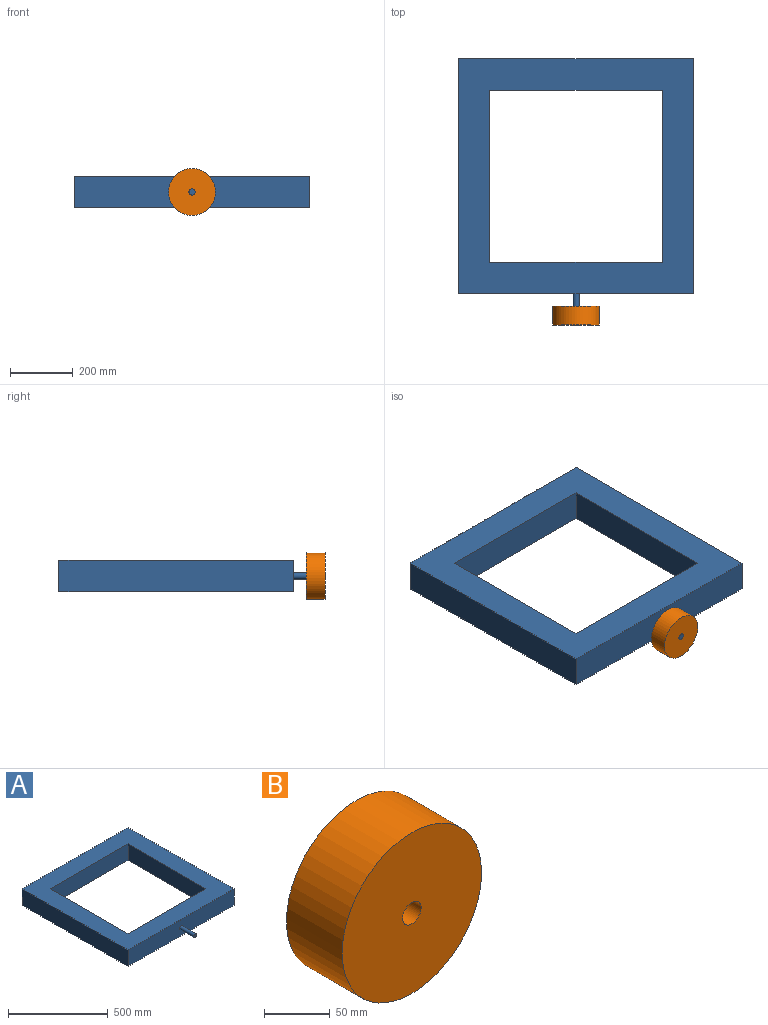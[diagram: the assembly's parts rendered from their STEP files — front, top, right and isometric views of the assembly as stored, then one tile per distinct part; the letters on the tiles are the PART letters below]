
ASSEMBLY  parts=2 mates=1
PART A: 12 faces, bbox 750x850x100 mm
  f0: plane 550x100mm, normal (0,1,0), area 55000mm2, adj f1,f7,f8,f9
  f1: plane 550x100mm, normal (1,0,0), area 55000mm2, adj f0,f2,f8,f9
  f2: plane 550x100mm, normal (0,-1,0), area 55000mm2, adj f1,f7,f8,f9
  f3: plane 750x100mm, normal (-1,0,0), area 75000mm2, adj f4,f6,f8,f9
  f4: plane 750x100mm, normal (0,-1,0), area 74685.8mm2, adj f3,f5,f8,f9,f10
  f5: plane 750x100mm, normal (1,0,0), area 75000mm2, adj f4,f6,f8,f9
  f6: plane 750x100mm, normal (0,1,0), area 75000mm2, adj f3,f5,f8,f9
  f7: plane 550x100mm, normal (-1,0,0), area 55000mm2, adj f0,f2,f8,f9
  f8: plane 750x750mm, normal (0,0,1), area 260000mm2, adj f0,f1,f2,f3,f4,f5,f6,f7
  f9: plane 750x750mm, normal (0,0,-1), area 260000mm2, adj f0,f1,f2,f3,f4,f5,f6,f7
  f10: cylinder r=10mm len=100mm, axis (0,1,0), area 6283.2mm2, adj f4,f11
  f11: plane 20x20mm, normal (0,-1,0), area 314.2mm2, adj f10
PART B: 4 faces, bbox 150x60x150 mm
  f0: plane 150x150mm, normal (0,1,0), area 17357.3mm2, adj f2,f3
  f1: plane 150x150mm, normal (0,-1,0), area 17357.3mm2, adj f2,f3
  f2: cylinder r=75mm len=150mm, axis (0,-1,0), area 28274.3mm2, adj f0,f1
  f3: cylinder r=10mm len=60mm, axis (0,-1,0), area 3769.9mm2, adj f0,f1
PLACE A t=(-674.22,322.75,942.35)mm
PLACE B t=(-429.84,235.75,992.35)mm
MATE revolute B.f2 <-> A.f10  axis (0,-1,0) through (-429.84,175.75,992.35)mm
